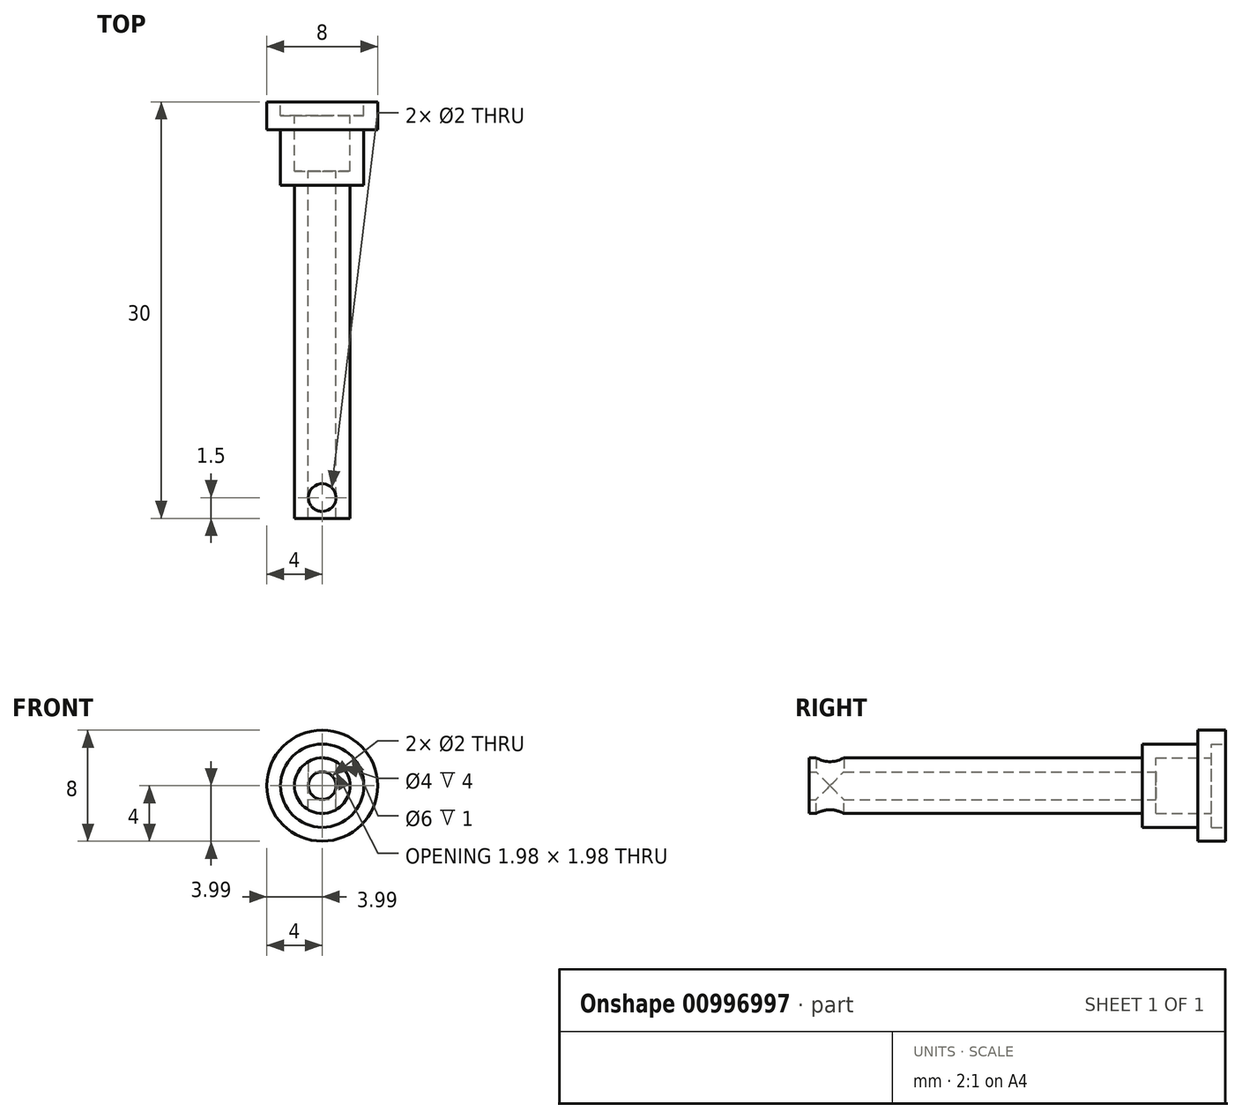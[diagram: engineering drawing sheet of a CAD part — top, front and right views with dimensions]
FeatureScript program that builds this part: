
annotation { "Feature Type Name" : "Feature", "Feature Type Description" : "" }
export const myFeature = defineFeature(function(context is Context, id is Id, definition is map)
    precondition{}
    {
        {
            var Q0;
            Q0=qCreatedBy(makeId("Front.planeOp"),FACE);
            var sketch = newSketch(context, id + "F0", { "sketchPlane" : qUnion([Q0])});
            skCircle(sketch, "E0", {"center": v(0, 0) * mm, "radius": 4 * mm});
            skCircle(sketch, "E1", {"center": v(0, 0) * mm, "radius": 3 * mm});
            skCircle(sketch, "E2", {"center": v(0, 0) * mm, "radius": 2 * mm});
            skCircle(sketch, "E3", {"center": v(0, 0) * mm, "radius": 1 * mm});
            skSolve(sketch);
        }
        {
            var Q0;
            Q0=makeQuery(id+"F0.imprint","IMPRINT",FACE,{"disambiguationData":[TD([[makeQuery(id+"F0.imprint","IMPRINT",EDGE,{"derivedFrom":sQuery(id+"F0.wireOp",EDGE,"E0")}),1.0]])]});
            extrude(context, id + "F1", {"entities" : qUnion([Q0]), "depth" : 2 * mm, "offsetDistance" : 25 * mm});
        }
        {
            var Q0;
            Q0=makeQuery(id+"F0.imprint","IMPRINT",FACE,{"disambiguationData":[TD([[makeQuery(id+"F0.imprint","IMPRINT",EDGE,{"derivedFrom":sQuery(id+"F0.wireOp",EDGE,"E1")}),1.0]])]});
            extrude(context, id + "F2", {"entities" : qUnion([Q0]), "operationType" : NewBodyOperationType.ADD, "depth" : 6 * mm, "offsetDistance" : 25 * mm, "hasSecondDirection" : true, "secondDirectionOppositeDirection" : false, "secondDirectionDepth" : 1 * mm});
        }
        {
            var Q0;
            Q0=makeQuery(id+"F0.imprint","IMPRINT",FACE,{"disambiguationData":[TD([[makeQuery(id+"F0.imprint","IMPRINT",EDGE,{"derivedFrom":sQuery(id+"F0.wireOp",EDGE,"E2")}),1.0]])]});
            extrude(context, id + "F3", {"entities" : qUnion([Q0]), "operationType" : NewBodyOperationType.ADD, "depth" : 30 * mm, "offsetDistance" : 25 * mm, "hasSecondDirection" : true, "secondDirectionOppositeDirection" : false, "secondDirectionDepth" : 5 * mm});
        }
        {
            var Q0;
            Q0=qCreatedBy(makeId("Top.planeOp"),FACE);
            var sketch = newSketch(context, id + "F4", { "sketchPlane" : qUnion([Q0])});
            skPoint(sketch, "E4", {"position": v(0, -28.5) * mm});
            skSolve(sketch);
        }
        {
            var Q0;
            Q0=sQuery(id+"F4.wireOp",VERTEX,"E4");
            var Q1;
            Q1=makeQuery(id+"F1.opExtrude","SWEPT_BODY",BODY,{"disambiguationData":[OSD([sQuery(id+"F0.wireOp",EDGE,"E0"),sQuery(id+"F0.wireOp",EDGE,"E1")])]});
            hole(context, id + "F5", {"style" : HoleStyle.SIMPLE, "endStyle" : HoleEndStyle.THROUGH, "holeDiameter" : 2 * mm, "majorDiameter" : 5 * mm, "isTappedThrough" : true, "tappedDepth" : 12 * mm, "tapClearance" : 3, "locations" : qUnion([Q0]), "scope" : qUnion([Q1])});
        }
        {
            var Q0;
            Q0=sQuery(id+"F4.wireOp",VERTEX,"E4");
            var Q1;
            Q1=makeQuery(id+"F1.opExtrude","SWEPT_BODY",BODY,{"disambiguationData":[OSD([sQuery(id+"F0.wireOp",EDGE,"E0"),sQuery(id+"F0.wireOp",EDGE,"E1")])]});
            hole(context, id + "F6", {"style" : HoleStyle.SIMPLE, "endStyle" : HoleEndStyle.THROUGH, "oppositeDirection" : true, "holeDiameter" : 2 * mm, "majorDiameter" : 5 * mm, "isTappedThrough" : true, "tappedDepth" : 12 * mm, "tapClearance" : 3, "locations" : qUnion([Q0]), "scope" : qUnion([Q1])});
        }
    });
